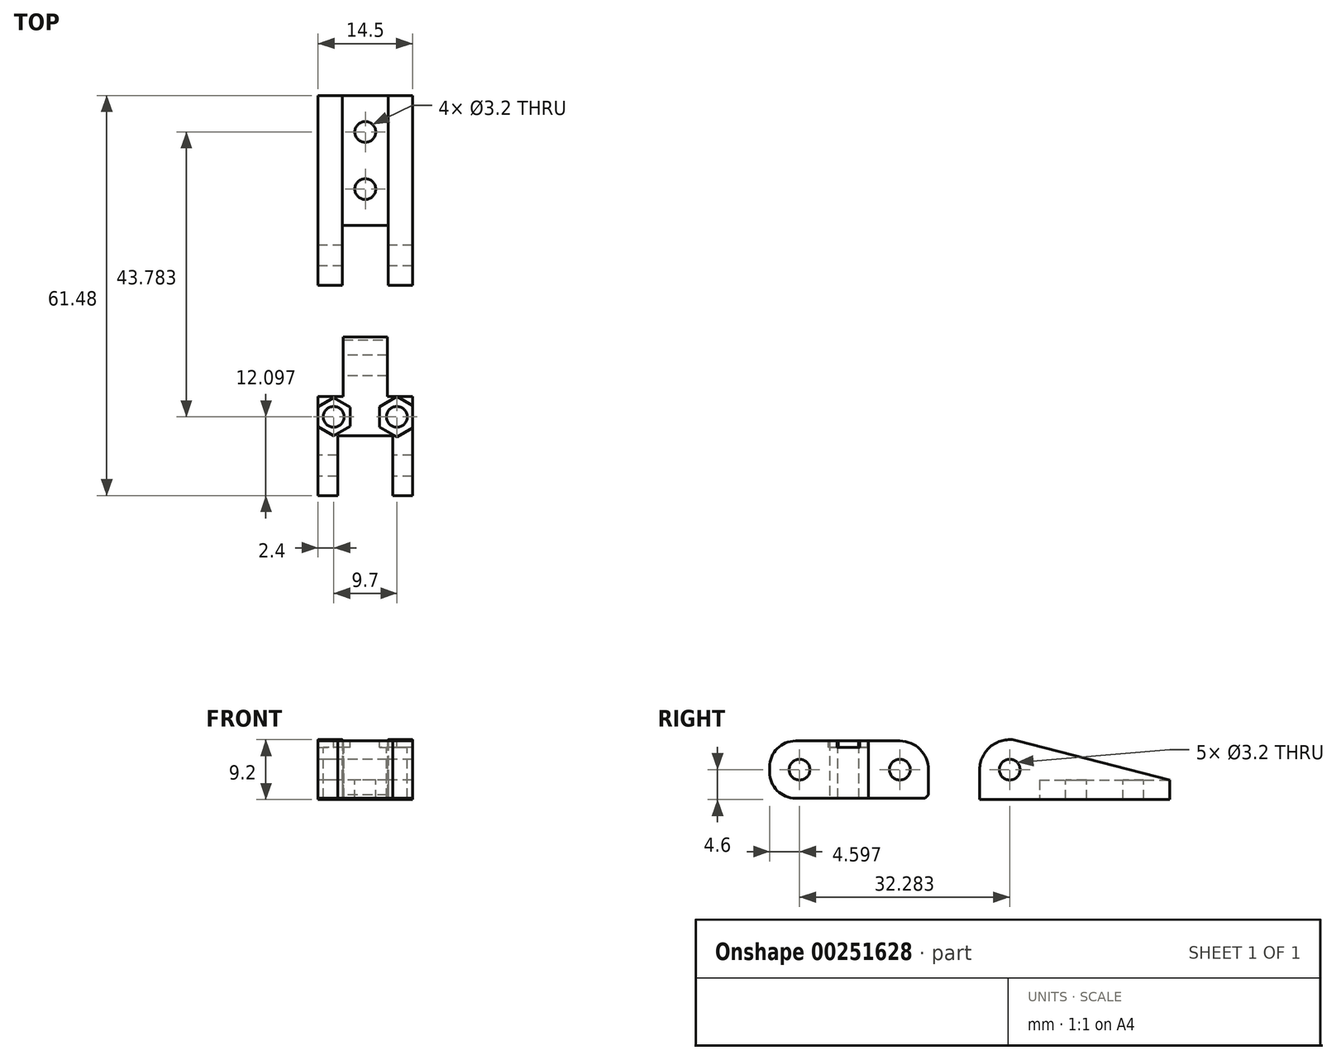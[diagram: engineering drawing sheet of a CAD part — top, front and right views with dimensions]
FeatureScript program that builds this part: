
annotation { "Feature Type Name" : "Feature", "Feature Type Description" : "" }
export const myFeature = defineFeature(function(context is Context, id is Id, definition is map)
    precondition{}
    {
        {
            var Q0;
            Q0=qCreatedBy(makeId("Right.planeOp"),FACE);
            var sketch = newSketch(context, id + "F0", { "sketchPlane" : qUnion([Q0])});
            skCircle(sketch, "E0", {"center": v(0, 0) * mm, "radius": 1.6 * mm});
            skCircle(sketch, "E1", {"center": v(0, 0) * mm, "radius": 4.6 * mm});
            skLineSegment(sketch, "E2", {"start": v(0, -4.6) * mm, "end": v(24.6, -4.6) * mm});
            skLineSegment(sketch, "E3", {"start": v(24.6, -4.6) * mm, "end": v(24.6, -1.6) * mm});
            skLineSegment(sketch, "E4", {"start": v(24.6, -1.6) * mm, "end": v(0, 4.75) * mm});
            skCircle(sketch, "E5", {"center": v(-16.88, 0) * mm, "radius": 1.6 * mm});
            skCircle(sketch, "E6", {"center": v(-16.88, 0) * mm, "radius": 4.4 * mm});
            skLineSegment(sketch, "E7", {"start": v(-16.88, -4.4) * mm, "end": v(-36.88, -4.4) * mm});
            skLineSegment(sketch, "E8", {"start": v(-36.88, -4.4) * mm, "end": v(-36.88, 4.4) * mm});
            skLineSegment(sketch, "E9", {"start": v(-36.88, 4.4) * mm, "end": v(-16.88, 4.4) * mm});
            skLineSegment(sketch, "E10", {"start": v(-16.88, -4.4) * mm, "end": v(-12.48, -4.4) * mm});
            skLineSegment(sketch, "E11", {"start": v(-12.48, -4.4) * mm, "end": v(-12.48, 0) * mm});
            skCircle(sketch, "E12", {"center": v(-32.28, 0) * mm, "radius": 1.6 * mm});
            skLineSegment(sketch, "E13", {"start": v(0, -4.6) * mm, "end": v(-4.6, -4.6) * mm});
            skLineSegment(sketch, "E14", {"start": v(-4.6, -4.6) * mm, "end": v(-4.6, 0) * mm});
            skSolve(sketch);
        }
        {
            var Q0;
            {var subQ1=sQuery(id+"F0.wireOp",EDGE,"E7");Q0=makeQuery(id+"F0.imprint","IMPRINT",FACE,{"disambiguationData":[TD([[makeQuery(id+"F0.imprint","IMPRINT",EDGE,{"derivedFrom":subQ1}),-1.0]])]});}
            var Q1;
            Q1=makeQuery(id+"F0.imprint","IMPRINT",FACE,{"disambiguationData":[TD([[makeQuery(id+"F0.imprint","IMPRINT",EDGE,{"derivedFrom":sQuery(id+"F0.wireOp",EDGE,"E5")}),-1.0]])]});
            var Q2;
            {var subQ0=sQuery(id+"F0.wireOp",EDGE,"E10");Q2=makeQuery(id+"F0.imprint","IMPRINT",FACE,{"disambiguationData":[TD([[makeQuery(id+"F0.imprint","IMPRINT",EDGE,{"derivedFrom":subQ0}),1.0]])]});}
            var Q3;
            Q3=makeQuery(id+"F0.imprint","IMPRINT",FACE,{"disambiguationData":[TD([[makeQuery(id+"F0.imprint","IMPRINT",EDGE,{"derivedFrom":sQuery(id+"F0.wireOp",EDGE,"E0")}),-1.0]])]});
            var Q4;
            {var subQ0=sQuery(id+"F0.wireOp",EDGE,"E2");Q4=makeQuery(id+"F0.imprint","IMPRINT",FACE,{"disambiguationData":[TD([[makeQuery(id+"F0.imprint","IMPRINT",EDGE,{"derivedFrom":subQ0}),1.0]])]});}
            var Q5;
            {var subQ0=sQuery(id+"F0.wireOp",EDGE,"E13");Q5=makeQuery(id+"F0.imprint","IMPRINT",FACE,{"disambiguationData":[TD([[makeQuery(id+"F0.imprint","IMPRINT",EDGE,{"derivedFrom":subQ0}),-1.0]])]});}
            extrude(context, id + "F1", {"entities" : qUnion([Q0, Q1, Q2, Q3, Q4, Q5]), "depth" : 14.5 * mm, "offsetDistance" : 25 * mm});
        }
        {
            var Q0;
            Q0=makeQuery(id+"F1.opExtrude","SWEPT_FACE",FACE,{"disambiguationData":[OSD([sQuery(id+"F0.wireOp",EDGE,"E2"),sQuery(id+"F0.wireOp",EDGE,"E13")])]});
            var sketch = newSketch(context, id + "F2", { "sketchPlane" : qUnion([Q0])});
            skLineSegment(sketch, "E15.0", {"start": v(14.5, 12.48) * mm, "end": v(0, 12.48) * mm});
            skLineSegment(sketch, "E16.0", {"start": v(14.5, 4.6) * mm, "end": v(0, 4.6) * mm});
            skLineSegment(sketch, "E17.0", {"start": v(0, 12.48) * mm, "end": v(0, 36.88) * mm});
            skLineSegment(sketch, "E18.0", {"start": v(14.5, 12.48) * mm, "end": v(14.5, 36.88) * mm});
            skLineSegment(sketch, "E19.0", {"start": v(14.5, 4.6) * mm, "end": v(14.5, -24.6) * mm});
            skLineSegment(sketch, "E20.0", {"start": v(0, 4.6) * mm, "end": v(0, -24.6) * mm});
            skLineSegment(sketch, "E21", {"start": v(3.75, -4.6) * mm, "end": v(10.75, -4.6) * mm});
            skLineSegment(sketch, "E22", {"start": v(10.75, -4.6) * mm, "end": v(10.75, 4.6) * mm});
            skLineSegment(sketch, "E23", {"start": v(3.75, -4.6) * mm, "end": v(3.75, 4.6) * mm});
            skLineSegment(sketch, "E24", {"start": v(3.85, 12.48) * mm, "end": v(3.85, 21.68) * mm});
            skLineSegment(sketch, "E25", {"start": v(3.85, 21.68) * mm, "end": v(10.65, 21.68) * mm});
            skLineSegment(sketch, "E26", {"start": v(10.65, 21.68) * mm, "end": v(10.65, 12.48) * mm});
            skLineSegment(sketch, "E27", {"start": v(3.85, 21.68) * mm, "end": v(0, 21.68) * mm});
            skLineSegment(sketch, "E28", {"start": v(10.65, 21.68) * mm, "end": v(14.5, 21.68) * mm});
            skLineSegment(sketch, "E29", {"start": v(3, 27.68) * mm, "end": v(11.5, 27.68) * mm});
            skLineSegment(sketch, "E30.0", {"start": v(14.5, 36.88) * mm, "end": v(0, 36.88) * mm});
            skLineSegment(sketch, "E31", {"start": v(7.25, 36.88) * mm, "end": v(7.25, 27.68) * mm, "construction": true});
            skLineSegment(sketch, "E32", {"start": v(3, 27.68) * mm, "end": v(3, 36.88) * mm});
            skLineSegment(sketch, "E33", {"start": v(11.5, 27.68) * mm, "end": v(11.5, 36.88) * mm});
            skSolve(sketch);
        }
        {
            var Q0;
            {var subQ3=sQuery(id+"F2.wireOp",EDGE,"E24");Q0=makeQuery(id+"F2.imprint","IMPRINT",FACE,{"disambiguationData":[TD([[makeQuery(id+"F2.imprint","IMPRINT",EDGE,{"derivedFrom":subQ3}),1.0]])]});}
            var Q1;
            {var subQ3=sQuery(id+"F2.wireOp",EDGE,"E26");Q1=makeQuery(id+"F2.imprint","IMPRINT",FACE,{"disambiguationData":[TD([[makeQuery(id+"F2.imprint","IMPRINT",EDGE,{"derivedFrom":subQ3}),1.0]])]});}
            var Q2;
            Q2=makeQuery(id+"F2.imprint","IMPRINT",FACE,{"disambiguationData":[TD([[makeQuery(id+"F2.imprint","IMPRINT",EDGE,{"derivedFrom":sQuery(id+"F2.wireOp",EDGE,"E21")}),1.0]])]});
            var Q3;
            Q3=makeQuery(id+"F2.imprint","IMPRINT",FACE,{"disambiguationData":[TD([[makeQuery(id+"F2.imprint","IMPRINT",EDGE,{"derivedFrom":sQuery(id+"F2.wireOp",EDGE,"E29")}),1.0]])]});
            var Q4;
            Q4=makeQuery(id+"F1.opExtrude","SWEPT_FACE",FACE,{"disambiguationData":[OSD([sQuery(id+"F0.wireOp",EDGE,"E4")])]});
            extrude(context, id + "F3", {"entities" : qUnion([Q0, Q1, Q2, Q3]), "operationType" : NewBodyOperationType.REMOVE, "endBound" : BoundingType.UP_TO_SURFACE, "oppositeDirection" : true, "depth" : 14.8 * mm, "endBoundEntityFace" : qUnion([Q4]), "offsetDistance" : 25 * mm});
        }
        {
            var Q0;
            Q0=makeQuery(id+"F1.opExtrude","SWEPT_FACE",FACE,{"disambiguationData":[OSD([sQuery(id+"F0.wireOp",EDGE,"E9")])]});
            var sketch = newSketch(context, id + "F4", { "sketchPlane" : qUnion([Q0])});
            skCircle(sketch, "E34", {"center": v(2.4, -24.78) * mm, "radius": 1.6 * mm});
            skCircle(sketch, "E35", {"center": v(12.1, -24.78) * mm, "radius": 1.6 * mm});
            skCircle(sketch, "E36.cCircle", {"center": v(2.4, -24.78) * mm, "radius": 2.54 * mm, "construction": true});
            skLineSegment(sketch, "E36.0", {"start": v(-0.14, -26.25) * mm, "end": v(-0.14, -23.32) * mm});
            skLineSegment(sketch, "E36.1", {"start": v(-0.14, -23.32) * mm, "end": v(2.4, -21.86) * mm});
            skLineSegment(sketch, "E36.2", {"start": v(2.4, -21.86) * mm, "end": v(4.94, -23.32) * mm});
            skLineSegment(sketch, "E36.3", {"start": v(4.94, -23.32) * mm, "end": v(4.94, -26.25) * mm});
            skLineSegment(sketch, "E36.4", {"start": v(4.94, -26.25) * mm, "end": v(2.4, -27.71) * mm});
            skLineSegment(sketch, "E36.5", {"start": v(2.4, -27.71) * mm, "end": v(-0.14, -26.25) * mm});
            skPoint(sketch, "E36.0.midPoint", {"position": v(-0.14, -24.78) * mm});
            skCircle(sketch, "E37.cCircle", {"center": v(12.1, -24.78) * mm, "radius": 2.69 * mm, "construction": true});
            skLineSegment(sketch, "E37.0", {"start": v(14.79, -23.23) * mm, "end": v(14.79, -26.34) * mm});
            skLineSegment(sketch, "E37.1", {"start": v(14.79, -26.34) * mm, "end": v(12.1, -27.89) * mm});
            skLineSegment(sketch, "E37.2", {"start": v(12.1, -27.89) * mm, "end": v(9.41, -26.34) * mm});
            skLineSegment(sketch, "E37.3", {"start": v(9.41, -26.34) * mm, "end": v(9.41, -23.23) * mm});
            skLineSegment(sketch, "E37.4", {"start": v(9.41, -23.23) * mm, "end": v(12.1, -21.68) * mm});
            skLineSegment(sketch, "E37.5", {"start": v(12.1, -21.68) * mm, "end": v(14.79, -23.23) * mm});
            skPoint(sketch, "E37.0.midPoint", {"position": v(14.79, -24.78) * mm});
            skSolve(sketch);
        }
        {
            var Q0;
            Q0=makeQuery(id+"F4.imprint","IMPRINT",FACE,{"disambiguationData":[TD([[makeQuery(id+"F4.imprint","IMPRINT",EDGE,{"derivedFrom":sQuery(id+"F4.wireOp",EDGE,"E34")}),1.0]])]});
            var Q1;
            Q1=makeQuery(id+"F4.imprint","IMPRINT",FACE,{"disambiguationData":[TD([[makeQuery(id+"F4.imprint","IMPRINT",EDGE,{"derivedFrom":sQuery(id+"F4.wireOp",EDGE,"E35")}),1.0]])]});
            var Q2;
            Q2=makeQuery(id+"F1.opExtrude","SWEPT_FACE",FACE,{"disambiguationData":[OSD([sQuery(id+"F0.wireOp",EDGE,"E7"),sQuery(id+"F0.wireOp",EDGE,"E10")])]});
            extrude(context, id + "F5", {"entities" : qUnion([Q0, Q1]), "operationType" : NewBodyOperationType.REMOVE, "endBound" : BoundingType.UP_TO_SURFACE, "oppositeDirection" : true, "depth" : 25 * mm, "endBoundEntityFace" : qUnion([Q2]), "offsetDistance" : 25 * mm});
        }
        {
            var Q0;
            Q0=makeQuery(id+"F4.imprint","IMPRINT",FACE,{"disambiguationData":[TD([[makeQuery(id+"F4.imprint","IMPRINT",EDGE,{"derivedFrom":sQuery(id+"F4.wireOp",EDGE,"E34")}),-1.0]])]});
            var Q1;
            Q1=makeQuery(id+"F4.imprint","IMPRINT",FACE,{"disambiguationData":[TD([[makeQuery(id+"F4.imprint","IMPRINT",EDGE,{"derivedFrom":sQuery(id+"F4.wireOp",EDGE,"E35")}),-1.0]])]});
            extrude(context, id + "F6", {"entities" : qUnion([Q0, Q1]), "operationType" : NewBodyOperationType.REMOVE, "oppositeDirection" : true, "depth" : 1 * mm, "offsetDistance" : 25 * mm});
        }
        {
            var Q0;
            {var subQ0=sQuery(id+"F0.wireOp",EDGE,"E9");var subQ1=sQuery(id+"F0.wireOp",EDGE,"E8");Q0=makeQuery(id+"F3.boolean.opBoolean","SPLIT",EDGE,{"disambiguationData":[TD([makeQuery(id+"F3.opExtrude","SWEPT_FACE",FACE,{"disambiguationData":[OSD([sQuery(id+"F2.wireOp",EDGE,"E33")])]})])],"derivedFrom":makeQuery(id+"F1.opExtrude","SWEPT_EDGE",EDGE,{"disambiguationData":[OSD([subQ1,subQ0])]})});}
            var Q1;
            {var subQ1=sQuery(id+"F0.wireOp",EDGE,"E8");var subQ2=sQuery(id+"F0.wireOp",EDGE,"E7");Q1=makeQuery(id+"F3.boolean.opBoolean","SPLIT",EDGE,{"disambiguationData":[TD([makeQuery(id+"F3.opExtrude","SWEPT_FACE",FACE,{"disambiguationData":[OSD([sQuery(id+"F2.wireOp",EDGE,"E33")])]})])],"derivedFrom":makeQuery(id+"F1.opExtrude","SWEPT_EDGE",EDGE,{"disambiguationData":[OSD([subQ2,subQ1])]})});}
            var Q2;
            {var subQ0=sQuery(id+"F0.wireOp",EDGE,"E9");var subQ1=sQuery(id+"F0.wireOp",EDGE,"E8");Q2=makeQuery(id+"F3.boolean.opBoolean","SPLIT",EDGE,{"disambiguationData":[TD([makeQuery(id+"F3.opExtrude","SWEPT_FACE",FACE,{"disambiguationData":[OSD([sQuery(id+"F2.wireOp",EDGE,"E32")])]})])],"derivedFrom":makeQuery(id+"F1.opExtrude","SWEPT_EDGE",EDGE,{"disambiguationData":[OSD([subQ1,subQ0])]})});}
            var Q3;
            {var subQ1=sQuery(id+"F0.wireOp",EDGE,"E8");var subQ2=sQuery(id+"F0.wireOp",EDGE,"E7");Q3=makeQuery(id+"F3.boolean.opBoolean","SPLIT",EDGE,{"disambiguationData":[TD([makeQuery(id+"F3.opExtrude","SWEPT_FACE",FACE,{"disambiguationData":[OSD([sQuery(id+"F2.wireOp",EDGE,"E32")])]})])],"derivedFrom":makeQuery(id+"F1.opExtrude","SWEPT_EDGE",EDGE,{"disambiguationData":[OSD([subQ2,subQ1])]})});}
            fillet(context, id + "F7", {"entities" : qUnion([Q0, Q1, Q2, Q3]), "tangentPropagation" : true, "radius" : 4 * mm, "defaultsChanged" : true, "vertexSettings" : [], "allowEdgeOverflow" : false});
        }
        {
            var Q0;
            Q0=makeQuery(id+"F1.opExtrude","SWEPT_FACE",FACE,{"disambiguationData":[OSD([sQuery(id+"F0.wireOp",EDGE,"E2"),sQuery(id+"F0.wireOp",EDGE,"E13")])]});
            cPlane(context, id + "F8", {"entities" : qUnion([Q0]), "cplaneType" : CPlaneType.OFFSET, "offset" : 8.17 * mm, "oppositeDirection" : true, "width" : 150 * mm, "height" : 150 * mm});
        }
        {
            var Q0;
            Q0=qCreatedBy(id+"F8.planeOp",FACE);
            var sketch = newSketch(context, id + "F9", { "sketchPlane" : qUnion([Q0])});
            skLineSegment(sketch, "E38.0", {"start": v(10.75, -4.6) * mm, "end": v(3.75, -4.6) * mm});
            skLineSegment(sketch, "E39.0", {"start": v(10.75, -24.6) * mm, "end": v(3.75, -24.6) * mm});
            skLineSegment(sketch, "E40", {"start": v(3.75, -4.6) * mm, "end": v(3.75, -24.6) * mm});
            skLineSegment(sketch, "E41", {"start": v(10.75, -4.6) * mm, "end": v(10.75, -24.6) * mm});
            skSolve(sketch);
        }
        {
            var Q0;
            Q0=makeQuery(id+"F9.imprint","IMPRINT",FACE,{"disambiguationData":[TD([[makeQuery(id+"F9.imprint","IMPRINT",EDGE,{"derivedFrom":sQuery(id+"F9.wireOp",EDGE,"E38.0")}),1.0]])]});
            var Q1;
            Q1=makeQuery(id+"F1.opExtrude","CAP_VERTEX",VERTEX,{"disambiguationData":[OSD([sQuery(id+"F0.wireOp",EDGE,"E3"),sQuery(id+"F0.wireOp",EDGE,"E4")])],"isStart":true});
            extrude(context, id + "F10", {"entities" : qUnion([Q0]), "operationType" : NewBodyOperationType.REMOVE, "endBound" : BoundingType.UP_TO_VERTEX, "depth" : 25 * mm, "endBoundEntityVertex" : qUnion([Q1]), "offsetDistance" : 25 * mm});
        }
        {
            var Q0;
            Q0=makeQuery(id+"F10.boolean.opBoolean","COPY",FACE,{"derivedFrom":makeQuery(id+"F10.opExtrude","CAP_FACE",FACE,{"disambiguationData":[OSD([sQuery(id+"F9.wireOp",EDGE,"E38.0"),sQuery(id+"F9.wireOp",EDGE,"E39.0"),sQuery(id+"F9.wireOp",EDGE,"E40"),sQuery(id+"F9.wireOp",EDGE,"E41")])],"isStart":false})});
            var sketch = newSketch(context, id + "F11", { "sketchPlane" : qUnion([Q0])});
            skCircle(sketch, "E42", {"center": v(7.25, 19) * mm, "radius": 1.6 * mm});
            skPoint(sketch, "E42.centerSnap0", {"position": v(7.25, 24.6) * mm});
            skCircle(sketch, "E43", {"center": v(7.25, 10.2) * mm, "radius": 1.6 * mm});
            skPoint(sketch, "E43.centerSnap0", {"position": v(7.25, 4.6) * mm});
            skSolve(sketch);
        }
        {
            var Q0;
            Q0=makeQuery(id+"F11.imprint","IMPRINT",FACE,{"disambiguationData":[TD([[makeQuery(id+"F11.imprint","IMPRINT",EDGE,{"derivedFrom":sQuery(id+"F11.wireOp",EDGE,"E42")}),1.0]])]});
            var Q1;
            Q1=makeQuery(id+"F11.imprint","IMPRINT",FACE,{"disambiguationData":[TD([[makeQuery(id+"F11.imprint","IMPRINT",EDGE,{"derivedFrom":sQuery(id+"F11.wireOp",EDGE,"E43")}),1.0]])]});
            var Q2;
            Q2=makeQuery(id+"F1.opExtrude","SWEPT_FACE",FACE,{"disambiguationData":[OSD([sQuery(id+"F0.wireOp",EDGE,"E2"),sQuery(id+"F0.wireOp",EDGE,"E13")])]});
            extrude(context, id + "F12", {"entities" : qUnion([Q0, Q1]), "operationType" : NewBodyOperationType.REMOVE, "endBound" : BoundingType.UP_TO_SURFACE, "oppositeDirection" : true, "depth" : 25 * mm, "endBoundEntityFace" : qUnion([Q2]), "offsetDistance" : 25 * mm});
        }
        {
            var Q0;
            Q0=makeQuery(id+"F1.opExtrude","SWEPT_EDGE",EDGE,{"disambiguationData":[OSD([sQuery(id+"F0.wireOp",EDGE,"E10"),sQuery(id+"F0.wireOp",EDGE,"E11")])]});
            chamfer(context, id + "F13", {"entities" : qUnion([Q0]), "width" : 0.5 * mm, "tangentPropagation" : true});
        }
    });
